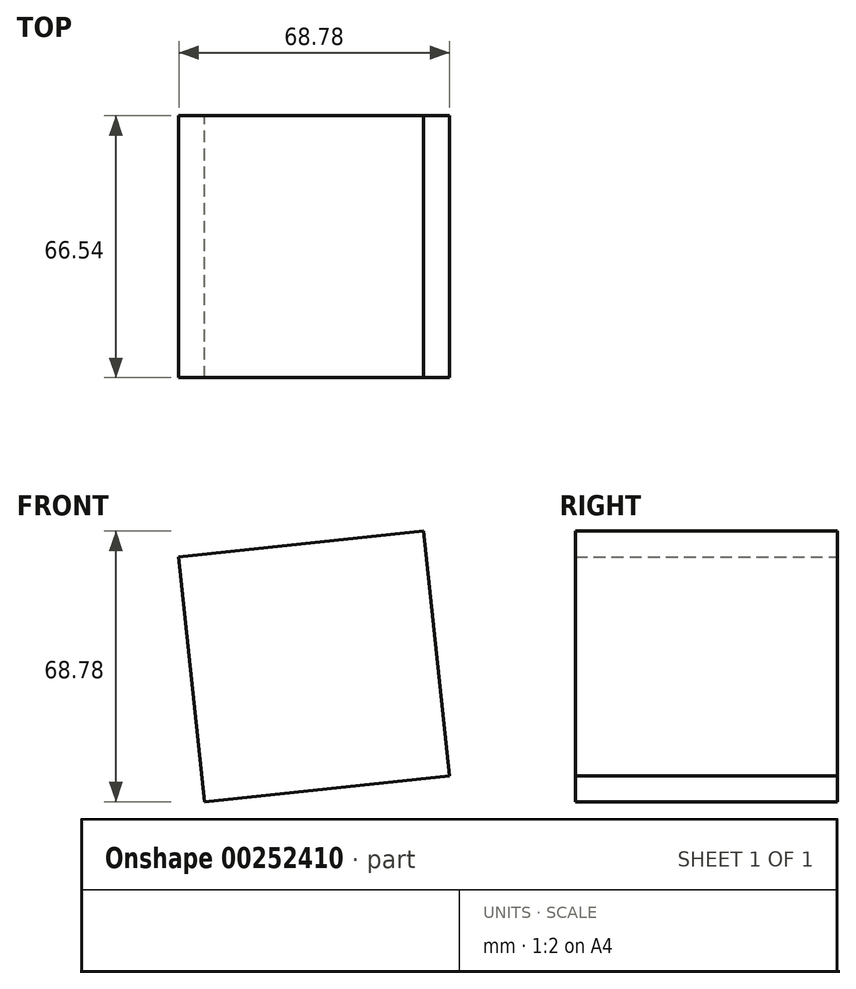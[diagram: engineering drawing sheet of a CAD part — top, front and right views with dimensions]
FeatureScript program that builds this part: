
annotation { "Feature Type Name" : "Feature", "Feature Type Description" : "" }
export const myFeature = defineFeature(function(context is Context, id is Id, definition is map)
    precondition{}
    {
        {
            var Q0;
            Q0=qCreatedBy(makeId("Front.planeOp"),FACE);
            var sketch = newSketch(context, id + "F0", { "sketchPlane" : qUnion([Q0])});
            skCircle(sketch, "E0.cCircle", {"center": v(0, 0) * mm, "radius": 44.25 * mm, "construction": true});
            skLineSegment(sketch, "E0.0", {"start": v(-34.4, 27.84) * mm, "end": v(27.84, 34.4) * mm});
            skLineSegment(sketch, "E0.1", {"start": v(27.84, 34.4) * mm, "end": v(34.4, -27.84) * mm});
            skLineSegment(sketch, "E0.2", {"start": v(34.4, -27.84) * mm, "end": v(-27.84, -34.4) * mm});
            skLineSegment(sketch, "E0.3", {"start": v(-27.84, -34.4) * mm, "end": v(-34.4, 27.84) * mm});
            skSolve(sketch);
        }
        {
            var Q0;
            Q0=makeQuery(id+"F0.imprint","IMPRINT",FACE,{"disambiguationData":[TD([[makeQuery(id+"F0.imprint","IMPRINT",EDGE,{"derivedFrom":sQuery(id+"F0.wireOp",EDGE,"E0.0")}),-1.0]])]});
            extrude(context, id + "F1", {"entities" : qUnion([Q0]), "endBound" : BoundingType.SYMMETRIC, "depth" : 66.55 * mm});
        }
    });
